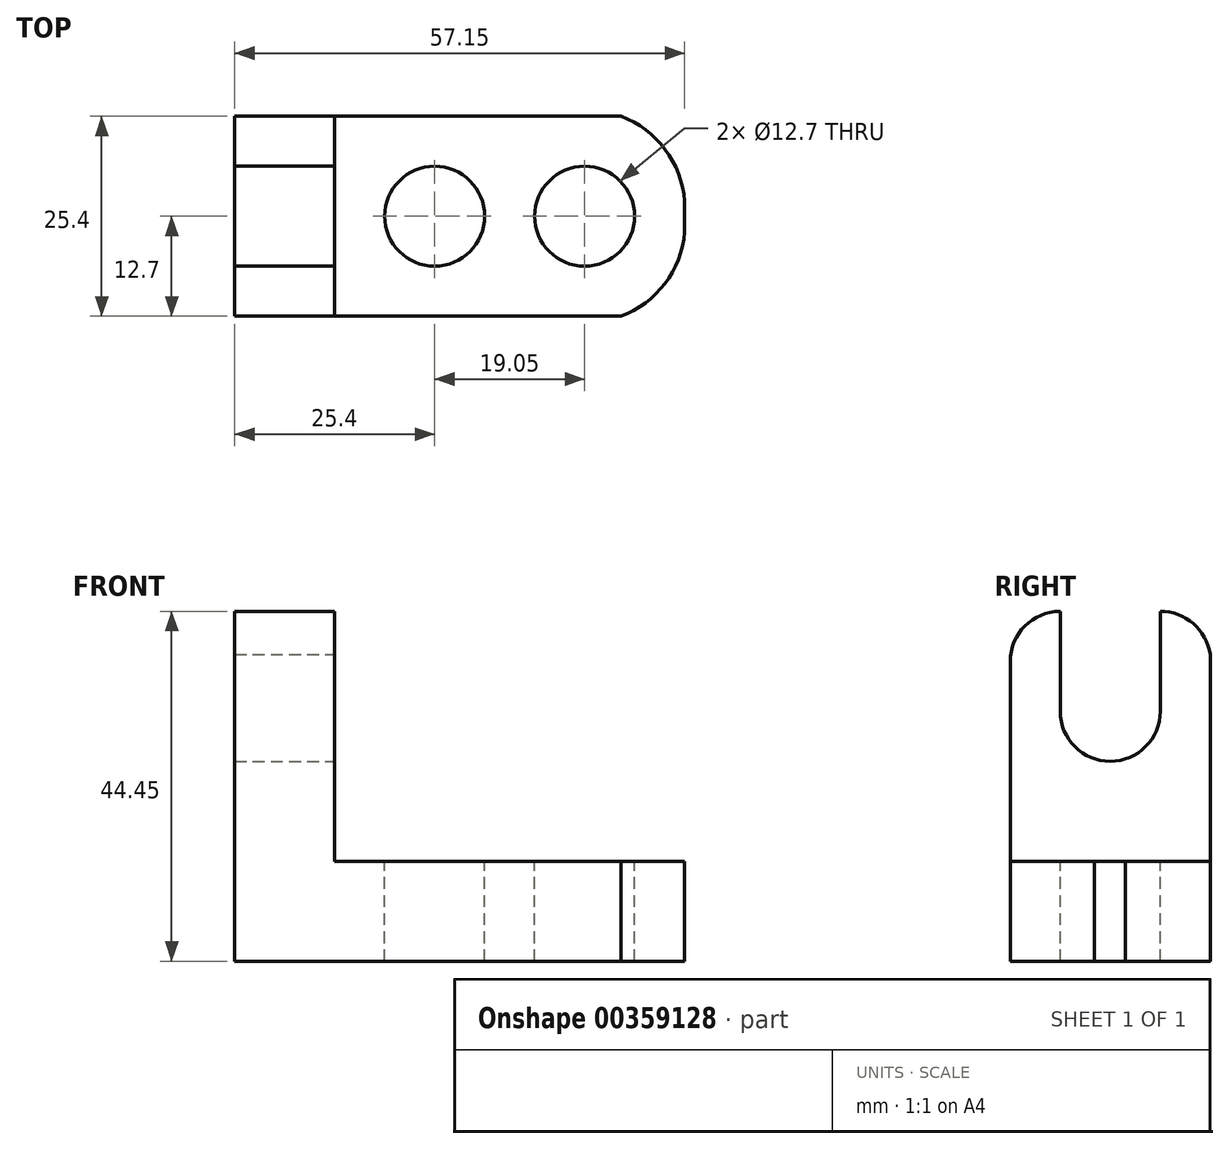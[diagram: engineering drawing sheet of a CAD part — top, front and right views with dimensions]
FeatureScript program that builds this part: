
annotation { "Feature Type Name" : "Feature", "Feature Type Description" : "" }
export const myFeature = defineFeature(function(context is Context, id is Id, definition is map)
    precondition{}
    {
        {
            var Q0;
            Q0=qCreatedBy(makeId("Front.planeOp"),FACE);
            var sketch = newSketch(context, id + "F0", { "sketchPlane" : qUnion([Q0])});
            skLineSegment(sketch, "E0", {"start": v(0, 0) * mm, "end": v(57.15, 0) * mm});
            skLineSegment(sketch, "E1", {"start": v(57.15, 0) * mm, "end": v(57.15, 12.7) * mm});
            skLineSegment(sketch, "E2", {"start": v(57.15, 12.7) * mm, "end": v(12.7, 12.7) * mm});
            skLineSegment(sketch, "E3", {"start": v(12.7, 12.7) * mm, "end": v(12.7, 44.45) * mm});
            skLineSegment(sketch, "E4", {"start": v(0, 44.45) * mm, "end": v(0, 0) * mm});
            skLineSegment(sketch, "E5", {"start": v(0, 44.45) * mm, "end": v(12.7, 44.45) * mm});
            skSolve(sketch);
        }
        {
            var Q0;
            Q0 = qSketchRegion(id + "F0", true);
            extrude(context, id + "F1", {"entities" : qUnion([Q0]), "depth" : 25.4 * mm});
        }
        {
            var Q0;
            Q0=makeQuery(id+"F1.opExtrude","SWEPT_FACE",FACE,{"disambiguationData":[OSD([sQuery(id+"F0.wireOp",EDGE,"E3")])]});
            var sketch = newSketch(context, id + "F2", { "sketchPlane" : qUnion([Q0])});
            skCircle(sketch, "E6", {"center": v(-12.7, 31.75) * mm, "radius": 6.35 * mm});
            skPoint(sketch, "E6.centerSnap0", {"position": v(-12.7, 44.45) * mm});
            skLineSegment(sketch, "E7", {"start": v(-19.05, 31.75) * mm, "end": v(-19.05, 44.45) * mm});
            skLineSegment(sketch, "E8", {"start": v(-19.05, 44.45) * mm, "end": v(-6.35, 44.45) * mm});
            skLineSegment(sketch, "E9", {"start": v(-6.35, 44.45) * mm, "end": v(-6.35, 31.75) * mm});
            skSolve(sketch);
        }
        {
            var Q0;
            Q0 = qSketchRegion(id + "F2", true);
            extrude(context, id + "F3", {"entities" : qUnion([Q0]), "operationType" : NewBodyOperationType.REMOVE, "oppositeDirection" : true, "depth" : 25.4 * mm});
        }
        {
            var Q0;
            Q0=makeQuery(id+"F1.opExtrude","SWEPT_FACE",FACE,{"disambiguationData":[OSD([sQuery(id+"F0.wireOp",EDGE,"E3")])]});
            var sketch = newSketch(context, id + "F4", { "sketchPlane" : qUnion([Q0])});
            skLineSegment(sketch, "E10", {"start": v(-25.4, 36.56) * mm, "end": v(-25.4, 44.45) * mm});
            skLineSegment(sketch, "E11", {"start": v(-25.4, 44.45) * mm, "end": v(-19.05, 44.45) * mm});
            skLineSegment(sketch, "E12", {"start": v(-6.35, 44.45) * mm, "end": v(0, 44.45) * mm});
            skLineSegment(sketch, "E13", {"start": v(0, 44.45) * mm, "end": v(0, 36.36) * mm});
            skArc(sketch, "E14", {"start": v(-19.05, 44.45) * mm, "mid": v(-23.54, 42.6) * mm, "end": v(-25.4, 38.1) * mm});
            skPoint(sketch, "E14.endSnap0", {"position": v(-19.05, 38.1) * mm});
            skArc(sketch, "E15", {"start": v(0, 38.97) * mm, "mid": v(-2.16, 42.9) * mm, "end": v(-6.35, 44.45) * mm});
            skSolve(sketch);
        }
        {
            var Q0;
            Q0 = qSketchRegion(id + "F4", true);
            extrude(context, id + "F5", {"entities" : qUnion([Q0]), "operationType" : NewBodyOperationType.REMOVE, "oppositeDirection" : true, "depth" : 25.4 * mm});
        }
        {
            var Q0;
            Q0=makeQuery(id+"F1.opExtrude","SWEPT_FACE",FACE,{"disambiguationData":[OSD([sQuery(id+"F0.wireOp",EDGE,"E2")])]});
            var sketch = newSketch(context, id + "F6", { "sketchPlane" : qUnion([Q0])});
            skCircle(sketch, "E16", {"center": v(44.45, -12.7) * mm, "radius": 6.35 * mm});
            skPoint(sketch, "E16.centerSnap0", {"position": v(57.15, -12.7) * mm});
            skCircle(sketch, "E17", {"center": v(25.4, -12.7) * mm, "radius": 6.35 * mm});
            skSolve(sketch);
        }
        {
            var Q0;
            Q0 = qSketchRegion(id + "F6", true);
            extrude(context, id + "F7", {"entities" : qUnion([Q0]), "operationType" : NewBodyOperationType.REMOVE, "oppositeDirection" : true, "depth" : 25.4 * mm});
        }
        {
            var Q0;
            Q0=makeQuery(id+"F1.opExtrude","SWEPT_FACE",FACE,{"disambiguationData":[OSD([sQuery(id+"F0.wireOp",EDGE,"E2")])]});
            var sketch = newSketch(context, id + "F8", { "sketchPlane" : qUnion([Q0])});
            skLineSegment(sketch, "E18", {"start": v(45.83, 0) * mm, "end": v(57.15, 0) * mm});
            skLineSegment(sketch, "E19", {"start": v(57.15, 0) * mm, "end": v(57.15, -25.4) * mm});
            skLineSegment(sketch, "E20", {"start": v(57.15, -25.4) * mm, "end": v(46.64, -25.4) * mm});
            skArc(sketch, "E21", {"start": v(57.15, -12.7) * mm, "mid": v(55.22, -5) * mm, "end": v(49.05, 0) * mm});
            skArc(sketch, "E22", {"start": v(49.05, -25.4) * mm, "mid": v(55.24, -20.41) * mm, "end": v(57.15, -12.7) * mm});
            skSolve(sketch);
        }
        {
            var Q0;
            Q0 = qSketchRegion(id + "F8", true);
            extrude(context, id + "F9", {"entities" : qUnion([Q0]), "operationType" : NewBodyOperationType.REMOVE, "oppositeDirection" : true, "depth" : 25.4 * mm});
        }
    });
